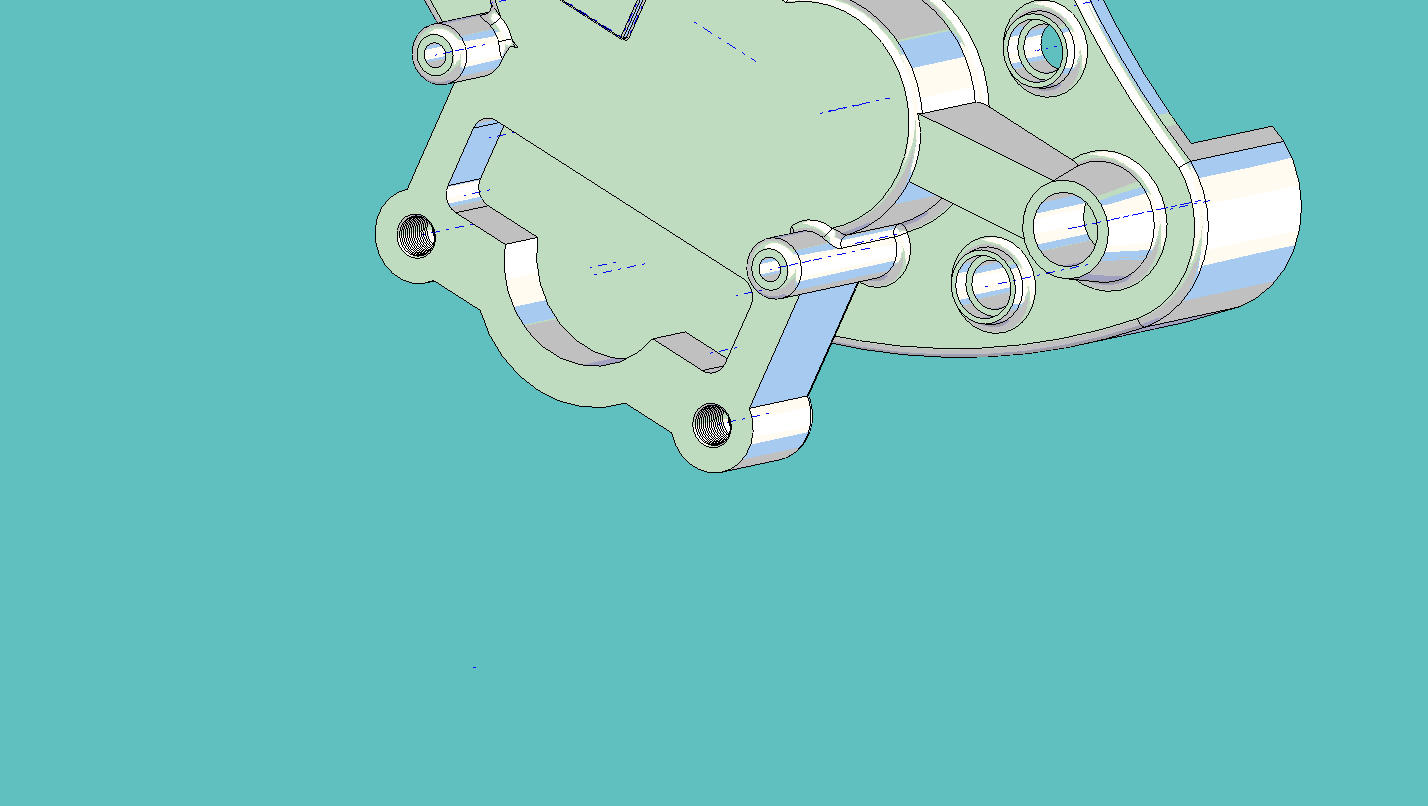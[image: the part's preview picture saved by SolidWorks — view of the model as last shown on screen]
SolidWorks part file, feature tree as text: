
SOLIDWORKS PART (.sldprt)
format: sldprt  version: not decoded by parser v0  size: 1,159,168 bytes
history: native  units: mm
features: sketch x29, cut_extrude x14, fillet x9, extrude x7, plane x5, mirror x4, sweep x2, pattern_linear x2, material x1, chamfer x1, delete_body x1 (+13 scaffold rows collapsed)
feature tree (88):
  scaffold x13  (default folders/planes/origin — collapsed)
  material  "Material <not specified>"
  sketch  "Sketch1"  dims[D1=63.5mm]
  extrude  "Extrude1"  Depth=31.75mm
  sketch  "Sketch5"  dims[D1=~43.962388mm]
  extrude  "Extrude2"  Depth=50.8mm
  sketch  "Sketch3"  dims[D1=50.0mm]
  cut_extrude  "Cut-Extrude1"  Depth=25.4mm
  sketch  "Sketch7"  dims[c1.D1=12.7mm c1.D2=12.7mm c2.D1=~13.906952mm c2.D2=25.0mm c2.D3=25.0mm c3.D1=~12.799272mm c3.D3=152.4mm]
  fillet  "Fillet1"  Radius=2.54mm
  fillet  "Fillet2"  Radius=2.54mm
  fillet  "Fillet3"  Radius=2.54mm
  sketch  "Sketch10"
  cut_extrude  "Cut-Extrude3"  [1 undecoded]
  plane  "Plane1"  Offset=10.16mm
  plane  "Plane2"  Offset=8.636mm
  sketch  "Sketch13"  dims[D1=273.05mm D2=137.16mm]
  cut_extrude  "Cut-Extrude4"  [1 undecoded]
  sketch  "Sketch14"
  cut_extrude  "Cut-Extrude5"  [1 undecoded]
  sketch  "Sketch15"
  extrude  "Extrude3"  Depth=53.18mm
  fillet  "Fillet4"  Radius=2.54mm
  sketch  "Sketch16"  dims[D1=~1.636236mm]
  cut_extrude  "Cut-Extrude6"  Depth=27.94mm
  fillet  "Fillet5"  Radius=2.54mm
  sketch  "Sketch17"
  extrude  "Extrude4"  Depth=2.54mm
  fillet  "Fillet6"  Radius=0.508mm
  chamfer  "Chamfer1"  Distance=1.27mm Angle=45deg
  sketch  "Sketch20"  dims[c1.D1=31.75mm c1.D2=25.4mm c2.D1=~20.003376mm]
  extrude  "Extrude5"  Depth=20.32mm
  cut_extrude  "Cut-Extrude8"  [1 undecoded]
  sketch  "Sketch21"  dims[D1=~4.108238mm]
  cut_extrude  "Cut-Extrude10"  Depth=25.4mm
  fillet  "Fillet7"  Radius=2.54mm
  sketch  "Sketch22"  dims[D1=10.16mm]
  cut_extrude  "Cut-Extrude11"  [1 undecoded]
  sketch  "Sketch24"
  cut_extrude  "Cut-Extrude12"  Depth=22.86mm
  sketch  "Sketch25"  dims[D1=20.574mm]
  extrude  "Extrude6"  Depth=5.08mm
  fillet  "Fillet8"  Radius=2.54mm
  sketch  "Sketch27"  dims[D1=~16.253517mm]
  cut_extrude  "Cut-Extrude15"  Depth=5.08mm
  mirror  "Mirror1"
  sketch  "Sketch29"  dims[D1=7.62mm]
  extrude  "Extrude7"  [1 undecoded]
  sketch  "Sketch30"
  sketch  "Sketch31"  dims[D1=5.08mm]
  cut_extrude  "Cut-Extrude18"  Depth=16.392582mm
  sketch  "Sketch32"  dims[D1=8.89mm]
  cut_extrude  "Cut-Extrude19"  Depth=16.392582mm
  cut_extrude  "Cut-Extrude20"  Depth=43.688mm
  sketch  "Sketch33"
  cut_extrude  "Cut-Extrude21"  Depth=59.69mm
  fillet  "Fillet11"  Radius=2.54mm
  plane  "Plane3"  Offset=94.488mm
  sketch  "Sketch34"  dims[D1=17.62mm]
  sketch  "Sketch36"
  mirror  "Rib3"
  sketch  "Sketch38"
  mirror  "Rib4"
  sketch  "Sketch40"
  mirror  "Rib5"
  delete_body  "Body-Delete1"
  plane  "Plane4"  Offset=50.8mm
  sketch  "Sketch42"
  sketch  "Sketch43"
  sweep  "Cut-Sweep1"
  pattern_linear  "LPattern1"  Count1=16 Count2=1 Spacing1=0.978mm Spacing2=50mm
  plane  "Plane5"  Offset=46.482mm
  sketch  "Sketch46"
  sketch  "Sketch47"
  sweep  "Cut-Sweep2"
  pattern_linear  "LPattern2"  Count1=16 Count2=1 Spacing1=0.978mm Spacing2=50mm
decode coverage: 42 of 69 modeling features carry decoded parameters
note: ~ marks probable driven/reference dimensions
note: 6 parameter values undecoded
summary: no parameter record found for 6 features
note: suppression state not decoded; provenance and decode notes live in map.json
